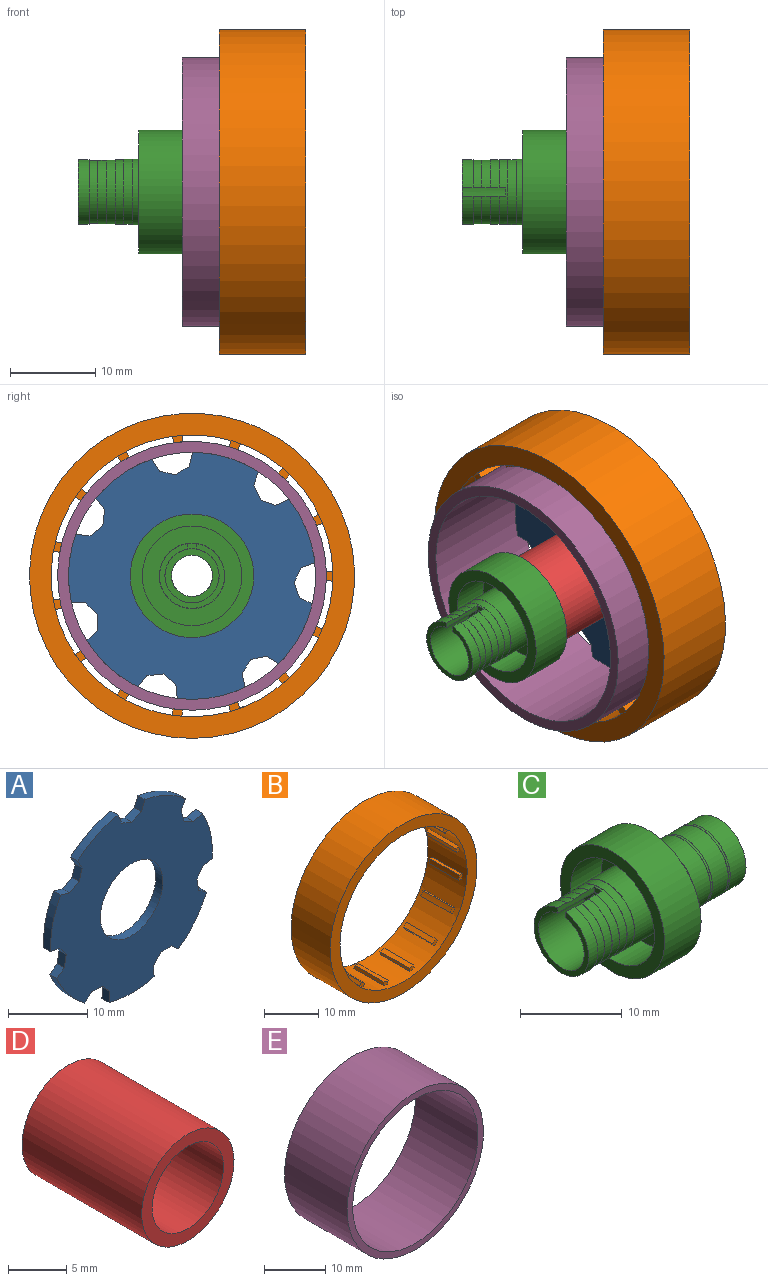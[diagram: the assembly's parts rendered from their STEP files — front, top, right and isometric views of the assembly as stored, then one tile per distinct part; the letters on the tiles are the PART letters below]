
ASSEMBLY  parts=5 mates=4
PART A: 38 faces, bbox 29x1.3x28.8 mm
  f0: plane 1.56x1.27mm, normal (0.92,0,0.38), area 2.1mm2, adj f1,f34,f36,f37
  f1: cylinder r=14.48mm len=7.26mm, axis (0,-1,0), area 10.4mm2, adj f0,f2,f36,f37
  f2: plane 1.48x1.27mm, normal (-0.88,0,-0.48), area 2.1mm2, adj f1,f3,f36,f37
  f3: plane 1.83x1.27mm, normal (-0.96,0,0.28), area 2.4mm2, adj f2,f4,f36,f37
  f4: plane 1.67x1.27mm, normal (-0.48,0,0.88), area 2.4mm2, adj f3,f5,f36,f37
  f5: plane 1.62x1.27mm, normal (0.28,0,0.96), area 2.1mm2, adj f4,f6,f36,f37
  f6: cylinder r=14.48mm len=7.85mm, axis (0,-1,0), area 10.4mm2, adj f5,f7,f36,f37
  f7: plane 1.66x1.27mm, normal (-0.17,0,-0.99), area 2.1mm2, adj f6,f8,f36,f37
  f8: plane 1.55x1.27mm, normal (-0.82,0,-0.58), area 2.4mm2, adj f7,f9,f36,f37
  f9: plane 1.88x1.27mm, normal (-0.99,0,0.17), area 2.4mm2, adj f8,f10,f36,f37
  f10: plane 1.38x1.27mm, normal (-0.58,0,0.82), area 2.1mm2, adj f9,f11,f36,f37
  f11: cylinder r=14.48mm len=6.3mm, axis (0,-1,0), area 10.4mm2, adj f10,f12,f36,f37
  f12: plane 1.27x1.26mm, normal (0.67,0,-0.75), area 2.1mm2, adj f11,f13,f36,f37
  f13: plane 1.9x1.27mm, normal (-0.06,0,-1), area 2.4mm2, adj f12,f14,f36,f37
  f14: plane 1.42x1.27mm, normal (-0.75,0,-0.67), area 2.4mm2, adj f13,f15,f36,f37
  f15: plane 1.68x1.27mm, normal (-1,0,0.06), area 2.1mm2, adj f14,f16,f36,f37
  f16: cylinder r=14.48mm len=8.05mm, axis (0,-1,0), area 10.4mm2, adj f15,f17,f36,f37
  f17: plane 1.68x1.27mm, normal (1,0,0.06), area 2.1mm2, adj f16,f18,f36,f37
  f18: plane 1.42x1.27mm, normal (0.75,0,-0.67), area 2.4mm2, adj f17,f19,f36,f37
  f19: plane 1.9x1.27mm, normal (0.06,0,-1), area 2.4mm2, adj f18,f20,f36,f37
  f20: plane 1.27x1.26mm, normal (-0.67,0,-0.75), area 2.1mm2, adj f19,f21,f36,f37
  f21: cylinder r=14.48mm len=6.3mm, axis (0,-1,0), area 10.4mm2, adj f20,f22,f36,f37
  f22: plane 1.38x1.27mm, normal (0.58,0,0.82), area 2.1mm2, adj f21,f23,f36,f37
  f23: plane 1.88x1.27mm, normal (0.99,0,0.17), area 2.4mm2, adj f22,f24,f36,f37
  f24: plane 1.55x1.27mm, normal (0.82,0,-0.58), area 2.4mm2, adj f23,f25,f36,f37
  f25: plane 1.66x1.27mm, normal (0.17,0,-0.99), area 2.1mm2, adj f24,f26,f36,f37
  f26: cylinder r=14.48mm len=7.85mm, axis (0,-1,0), area 10.4mm2, adj f25,f27,f36,f37
  f27: plane 1.62x1.27mm, normal (-0.28,0,0.96), area 2.1mm2, adj f26,f28,f36,f37
  f28: plane 1.67x1.27mm, normal (0.48,0,0.88), area 2.4mm2, adj f27,f29,f36,f37
  f29: plane 1.83x1.27mm, normal (0.96,0,0.28), area 2.4mm2, adj f28,f30,f36,f37
  f30: plane 1.48x1.27mm, normal (0.88,0,-0.48), area 2.1mm2, adj f29,f31,f36,f37
  f31: cylinder r=14.48mm len=7.26mm, axis (0,-1,0), area 10.4mm2, adj f30,f32,f36,f37
  f32: plane 1.56x1.27mm, normal (-0.92,0,0.38), area 2.1mm2, adj f31,f33,f36,f37
  f33: plane 1.76x1.27mm, normal (-0.38,0,0.92), area 2.4mm2, adj f32,f34,f36,f37
  f34: plane 1.76x1.27mm, normal (0.38,0,0.92), area 2.4mm2, adj f0,f33,f36,f37
  f35: cylinder r=5.59mm len=11.18mm, axis (0,-1,0), area 44.6mm2, adj f36,f37
  f36: plane 28.96x28.75mm, normal (0,1,0), area 501.5mm2, adj f0,f1,f2,f3,f4,f5,f6,f7
  f37: plane 28.96x28.75mm, normal (0,-1,0), area 501.5mm2, adj f0,f1,f2,f3,f4,f5,f6,f7
PART B: 79 faces, bbox 38.1x10.2x38.1 mm
  f0: cylinder r=15.75mm len=7.62mm, axis (0,1,0), area 8.4mm2, adj f1,f2,f3,f4
  f1: plane 7.62x0.69mm, normal (0.9,0,-0.44), area 5.8mm2, adj f0,f3,f4,f70
  f2: plane 7.62x0.71mm, normal (-0.93,0,0.37), area 5.8mm2, adj f0,f3,f4,f70
  f3: plane 1.34x1.15mm, normal (0,1,0), area 0.9mm2, adj f0,f1,f2,f70
  f4: plane 1.34x1.15mm, normal (0,-1,0), area 0.9mm2, adj f0,f1,f2,f70
  f5: cylinder r=15.75mm len=7.62mm, axis (0,1,0), area 8.4mm2, adj f6,f7,f8,f9
  f6: plane 7.62x0.58mm, normal (0.64,0,-0.77), area 5.8mm2, adj f5,f8,f9,f70
  f7: plane 7.62x0.55mm, normal (-0.69,0,0.72), area 5.8mm2, adj f5,f8,f9,f70
  f8: plane 1.35x1.32mm, normal (0,1,0), area 0.9mm2, adj f5,f6,f7,f70
  f9: plane 1.35x1.32mm, normal (0,-1,0), area 0.9mm2, adj f5,f6,f7,f70
  f10: cylinder r=15.75mm len=7.62mm, axis (0,1,0), area 8.4mm2, adj f11,f12,f13,f14
  f11: plane 7.62x0.73mm, normal (0.28,0,-0.96), area 5.8mm2, adj f10,f13,f14,f70
  f12: plane 7.62x0.72mm, normal (-0.34,0,0.94), area 5.8mm2, adj f10,f13,f14,f70
  f13: plane 1.31x1.07mm, normal (0,1,0), area 0.9mm2, adj f10,f11,f12,f70
  f14: plane 1.31x1.07mm, normal (0,-1,0), area 0.9mm2, adj f10,f11,f12,f70
  f15: cylinder r=15.75mm len=7.62mm, axis (0,1,0), area 8.4mm2, adj f16,f17,f18,f19
  f16: plane 7.62x0.75mm, normal (-0.14,0,-0.99), area 5.8mm2, adj f15,f18,f19,f70
  f17: plane 7.62x0.76mm, normal (0.07,0,1), area 5.8mm2, adj f15,f18,f19,f70
  f18: plane 1.2x0.88mm, normal (0,1,0), area 0.9mm2, adj f15,f16,f17,f70
  f19: plane 1.2x0.88mm, normal (0,-1,0), area 0.9mm2, adj f15,f16,f17,f70
  f20: cylinder r=15.75mm len=7.62mm, axis (0,1,0), area 8.4mm2, adj f21,f22,f23,f24
  f21: plane 7.62x0.65mm, normal (-0.53,0,-0.85), area 5.8mm2, adj f20,f23,f24,f70
  f22: plane 7.62x0.67mm, normal (0.47,0,0.88), area 5.8mm2, adj f20,f23,f24,f70
  f23: plane 1.36x1.22mm, normal (0,1,0), area 0.9mm2, adj f20,f21,f22,f70
  f24: plane 1.36x1.22mm, normal (0,-1,0), area 0.9mm2, adj f20,f21,f22,f70
  f25: cylinder r=15.75mm len=7.62mm, axis (0,1,0), area 8.4mm2, adj f26,f27,f28,f29
  f26: plane 7.62x0.63mm, normal (-0.83,0,-0.56), area 5.8mm2, adj f25,f28,f29,f70
  f27: plane 7.62x0.6mm, normal (0.79,0,0.62), area 5.8mm2, adj f25,f28,f29,f70
  f28: plane 1.36x1.28mm, normal (0,1,0), area 0.9mm2, adj f25,f26,f27,f70
  f29: plane 1.36x1.28mm, normal (0,-1,0), area 0.9mm2, adj f25,f26,f27,f70
  f30: cylinder r=15.75mm len=7.62mm, axis (0,1,0), area 8.4mm2, adj f31,f32,f33,f34
  f31: plane 7.62x0.75mm, normal (-0.98,0,-0.17), area 5.8mm2, adj f30,f33,f34,f70
  f32: plane 7.62x0.74mm, normal (0.97,0,0.24), area 5.8mm2, adj f30,f33,f34,f70
  f33: plane 1.26x0.98mm, normal (0,1,0), area 0.9mm2, adj f30,f31,f32,f70
  f34: plane 1.26x0.98mm, normal (0,-1,0), area 0.9mm2, adj f30,f31,f32,f70
  f35: cylinder r=15.75mm len=7.62mm, axis (0,1,0), area 8.4mm2, adj f36,f37,f38,f39
  f36: plane 7.62x0.74mm, normal (-0.97,0,0.24), area 5.8mm2, adj f35,f38,f39,f70
  f37: plane 7.62x0.75mm, normal (0.98,0,-0.17), area 5.8mm2, adj f35,f38,f39,f70
  f38: plane 1.26x0.98mm, normal (0,1,0), area 0.9mm2, adj f35,f36,f37,f70
  f39: plane 1.26x0.98mm, normal (0,-1,0), area 0.9mm2, adj f35,f36,f37,f70
  f40: cylinder r=15.75mm len=7.62mm, axis (0,1,0), area 8.4mm2, adj f41,f42,f43,f44
  f41: plane 7.62x0.6mm, normal (-0.79,0,0.62), area 5.8mm2, adj f40,f43,f44,f70
  f42: plane 7.62x0.63mm, normal (0.83,0,-0.56), area 5.8mm2, adj f40,f43,f44,f70
  f43: plane 1.36x1.28mm, normal (0,1,0), area 0.9mm2, adj f40,f41,f42,f70
  f44: plane 1.36x1.28mm, normal (0,-1,0), area 0.9mm2, adj f40,f41,f42,f70
  f45: cylinder r=15.75mm len=7.62mm, axis (0,1,0), area 8.4mm2, adj f46,f47,f48,f49
  f46: plane 7.62x0.67mm, normal (-0.47,0,0.88), area 5.8mm2, adj f45,f48,f49,f70
  f47: plane 7.62x0.65mm, normal (0.53,0,-0.85), area 5.8mm2, adj f45,f48,f49,f70
  f48: plane 1.36x1.22mm, normal (0,1,0), area 0.9mm2, adj f45,f46,f47,f70
  f49: plane 1.36x1.22mm, normal (0,-1,0), area 0.9mm2, adj f45,f46,f47,f70
  f50: cylinder r=15.75mm len=7.62mm, axis (0,1,0), area 8.4mm2, adj f51,f52,f53,f54
  f51: plane 7.62x0.76mm, normal (-0.07,0,1), area 5.8mm2, adj f50,f53,f54,f70
  f52: plane 7.62x0.75mm, normal (0.14,0,-0.99), area 5.8mm2, adj f50,f53,f54,f70
  f53: plane 1.2x0.88mm, normal (0,1,0), area 0.9mm2, adj f50,f51,f52,f70
  f54: plane 1.2x0.88mm, normal (0,-1,0), area 0.9mm2, adj f50,f51,f52,f70
  f55: cylinder r=15.75mm len=7.62mm, axis (0,1,0), area 8.4mm2, adj f56,f57,f58,f59
  f56: plane 7.62x0.72mm, normal (0.34,0,0.94), area 5.8mm2, adj f55,f58,f59,f70
  f57: plane 7.62x0.73mm, normal (-0.28,0,-0.96), area 5.8mm2, adj f55,f58,f59,f70
  f58: plane 1.31x1.07mm, normal (0,1,0), area 0.9mm2, adj f55,f56,f57,f70
  f59: plane 1.31x1.07mm, normal (0,-1,0), area 0.9mm2, adj f55,f56,f57,f70
  f60: cylinder r=15.75mm len=7.62mm, axis (0,1,0), area 8.4mm2, adj f61,f62,f63,f64
  f61: plane 7.62x0.55mm, normal (0.69,0,0.72), area 5.8mm2, adj f60,f63,f64,f70
  f62: plane 7.62x0.58mm, normal (-0.64,0,-0.77), area 5.8mm2, adj f60,f63,f64,f70
  f63: plane 1.35x1.32mm, normal (0,1,0), area 0.9mm2, adj f60,f61,f62,f70
  f64: plane 1.35x1.32mm, normal (0,-1,0), area 0.9mm2, adj f60,f61,f62,f70
  f65: cylinder r=15.75mm len=7.62mm, axis (0,1,0), area 8.4mm2, adj f66,f67,f68,f69
  f66: plane 7.62x0.71mm, normal (0.93,0,0.37), area 5.8mm2, adj f65,f68,f69,f70
  f67: plane 7.62x0.69mm, normal (-0.9,0,-0.44), area 5.8mm2, adj f65,f68,f69,f70
  f68: plane 1.34x1.15mm, normal (0,1,0), area 0.9mm2, adj f65,f66,f67,f70
  f69: plane 1.34x1.15mm, normal (0,-1,0), area 0.9mm2, adj f65,f66,f67,f70
  f70: cylinder r=16.51mm len=33.02mm, axis (0,1,0), area 922.2mm2, adj f1,f2,f3,f4,f6,f7,f8,f9
  f71: cylinder r=19.05mm len=38.1mm, axis (0,1,0), area 1216.1mm2, adj f72,f73
  f72: plane 38.1x38.1mm, normal (0,-1,0), area 283.8mm2, adj f70,f71
  f73: plane 38.1x38.1mm, normal (0,1,0), area 283.8mm2, adj f70,f71
  f74: cylinder r=15.75mm len=7.62mm, axis (0,1,0), area 8.4mm2, adj f75,f76,f77,f78
  f75: plane 7.62x0.76mm, normal (1,0,-0.03), area 5.8mm2, adj f70,f74,f77,f78
  f76: plane 7.62x0.76mm, normal (-1,0,-0.03), area 5.8mm2, adj f70,f74,f77,f78
  f77: plane 1.15x0.77mm, normal (0,-1,0), area 0.9mm2, adj f70,f74,f75,f76
  f78: plane 1.15x0.77mm, normal (0,1,0), area 0.9mm2, adj f70,f74,f75,f76
PART C: 42 faces, bbox 21.8x14.5x14.5 mm
  f0: plane 7.47x7.43mm, normal (-1,0,0), area 0.6mm2, adj f1,f10,f40,f41
  f1: cylinder r=3.71mm len=7.42mm, axis (-1,0,0), area 22.6mm2, adj f0,f2,f40,f41
  f2: plane 7.62x7.59mm, normal (1,0,0), area 2.3mm2, adj f1,f3,f40,f41
  f3: cylinder r=3.81mm len=7.62mm, axis (-1,0,0), area 29.1mm2, adj f2,f4,f40,f41
  f4: plane 7.62x7.59mm, normal (-1,0,0), area 13.3mm2, adj f3,f5,f40,f41
  f5: cylinder r=3.17mm len=6.35mm, axis (-1,0,0), area 121.5mm2, adj f4,f11,f39,f40,f41
  f6: cylinder r=3.78mm len=7.57mm, axis (-1,0,0), area 23.4mm2, adj f7,f38,f39,f40,f41
  f7: plane 7.57x7.54mm, normal (-1,0,0), area 0.6mm2, adj f6,f8,f40,f41
  f8: cylinder r=3.76mm len=7.52mm, axis (-1,0,0), area 23mm2, adj f7,f9,f40,f41
  f9: plane 7.52x7.48mm, normal (-1,0,0), area 0.6mm2, adj f8,f10,f40,f41
  f10: cylinder r=3.73mm len=7.47mm, axis (-1,0,0), area 22.8mm2, adj f0,f9,f40,f41
  f11: plane 6.35x6.35mm, normal (-1,0,0), area 13.4mm2, adj f5,f12
  f12: cylinder r=2.41mm len=5.84mm, axis (-1,0,0), area 88.6mm2, adj f11,f13
  f13: cone r=2.44mm half-angle=0.2deg, axis (1,0,0), area 127.8mm2, adj f12,f14
  f14: plane 6.4x6.4mm, normal (1,0,0), area 13.5mm2, adj f13,f15
  f15: cylinder r=3.2mm len=6.4mm, axis (-1,0,0), area 25.5mm2, adj f14,f16
  f16: plane 7.67x7.67mm, normal (1,0,0), area 14mm2, adj f15,f17
  f17: cylinder r=3.84mm len=7.67mm, axis (-1,0,0), area 53.6mm2, adj f16,f18
  f18: plane 7.72x7.72mm, normal (1,0,0), area 0.6mm2, adj f17,f19
  f19: cylinder r=3.86mm len=7.72mm, axis (-1,0,0), area 6.2mm2, adj f18,f20
  f20: plane 7.72x7.72mm, normal (-1,0,0), area 0.6mm2, adj f19,f21
  f21: cylinder r=3.84mm len=7.67mm, axis (-1,0,0), area 53.6mm2, adj f20,f22
  f22: plane 7.72x7.72mm, normal (1,0,0), area 0.6mm2, adj f21,f23
  f23: cylinder r=3.86mm len=7.72mm, axis (-1,0,0), area 6.2mm2, adj f22,f24
  f24: plane 7.72x7.72mm, normal (-1,0,0), area 0.6mm2, adj f23,f25
  f25: cylinder r=3.84mm len=7.67mm, axis (-1,0,0), area 53.6mm2, adj f24,f26
  f26: plane 7.72x7.72mm, normal (1,0,0), area 0.6mm2, adj f25,f27
  f27: cylinder r=3.86mm len=7.72mm, axis (-1,0,0), area 6.2mm2, adj f26,f28
  f28: plane 7.72x7.72mm, normal (-1,0,0), area 0.6mm2, adj f27,f29
  f29: cylinder r=3.84mm len=7.67mm, axis (-1,0,0), area 53.6mm2, adj f28,f30
  f30: plane 14.48x14.48mm, normal (1,0,0), area 118.4mm2, adj f29,f31
  f31: cylinder r=7.24mm len=14.48mm, axis (-1,0,0), area 231.1mm2, adj f30,f32
  f32: plane 14.48x14.48mm, normal (-1,0,0), area 57.4mm2, adj f31,f33
  f33: cylinder r=5.84mm len=11.68mm, axis (-1,0,0), area 158.5mm2, adj f32,f34
  f34: plane 11.68x11.68mm, normal (-1,0,0), area 61mm2, adj f33,f35
  f35: cylinder r=3.84mm len=7.67mm, axis (-1,0,0), area 122.4mm2, adj f34,f36
  f36: plane 7.67x7.67mm, normal (-1,0,0), area 0.6mm2, adj f35,f37
  f37: cylinder r=3.81mm len=7.62mm, axis (-1,0,0), area 24.3mm2, adj f36,f38
  f38: plane 7.62x7.62mm, normal (-1,0,0), area 0.6mm2, adj f6,f37
  f39: plane 1.02x0.65mm, normal (-1,0,0), area 0.6mm2, adj f5,f6,f40,f41
  f40: plane 5.08x0.64mm, normal (0,-1,0), area 3mm2, adj f0,f1,f2,f3,f4,f5,f6,f7
  f41: plane 5.08x0.64mm, normal (0,1,0), area 3mm2, adj f0,f1,f2,f3,f4,f5,f6,f7
PART D: 4 faces, bbox 11.2x14.5x11.2 mm
  f0: cylinder r=4.32mm len=14.48mm, axis (0,1,0), area 392.8mm2, adj f2,f3
  f1: cylinder r=5.59mm len=14.48mm, axis (0,1,0), area 508.3mm2, adj f2,f3
  f2: plane 11.18x11.18mm, normal (0,-1,0), area 39.5mm2, adj f0,f1
  f3: plane 11.18x11.18mm, normal (0,1,0), area 39.5mm2, adj f0,f1
PART E: 4 faces, bbox 31.5x14.5x31.5 mm
  f0: cylinder r=14.48mm len=28.96mm, axis (0,1,0), area 1317mm2, adj f2,f3
  f1: cylinder r=15.75mm len=31.5mm, axis (0,1,0), area 1432.6mm2, adj f2,f3
  f2: plane 31.5x31.5mm, normal (0,-1,0), area 120.6mm2, adj f0,f1
  f3: plane 31.5x31.5mm, normal (0,1,0), area 120.6mm2, adj f0,f1
PLACE A rot(axis=(0.34,-0.34,0.88),97.4deg) t=(12.57,28.52,0.6)mm
PLACE B rot(axis=(0.34,-0.34,0.88),97.4deg) t=(7.49,28.52,0.6)mm
PLACE C t=(-9.02,28.52,0.6)mm fixed
PLACE D rot(axis=(0.34,-0.34,0.88),97.4deg) t=(-1.91,28.52,0.6)mm
PLACE E rot(axis=(0.34,-0.34,0.88),97.4deg) t=(-1.91,28.52,0.6)mm
MATE fastened E.f1 <-> B.f71  axis (1,0,0) through (12.57,28.52,0.6)mm
MATE fastened D.f1 <-> A.f35  axis (1,0,0) through (12.57,28.52,0.6)mm
MATE revolute D.f1 <-> C.f1  axis (-1,0,0) through (-1.91,28.52,0.6)mm
MATE fastened D.f1 <-> E.f0  axis (1,0,0) through (12.57,28.52,0.6)mm
